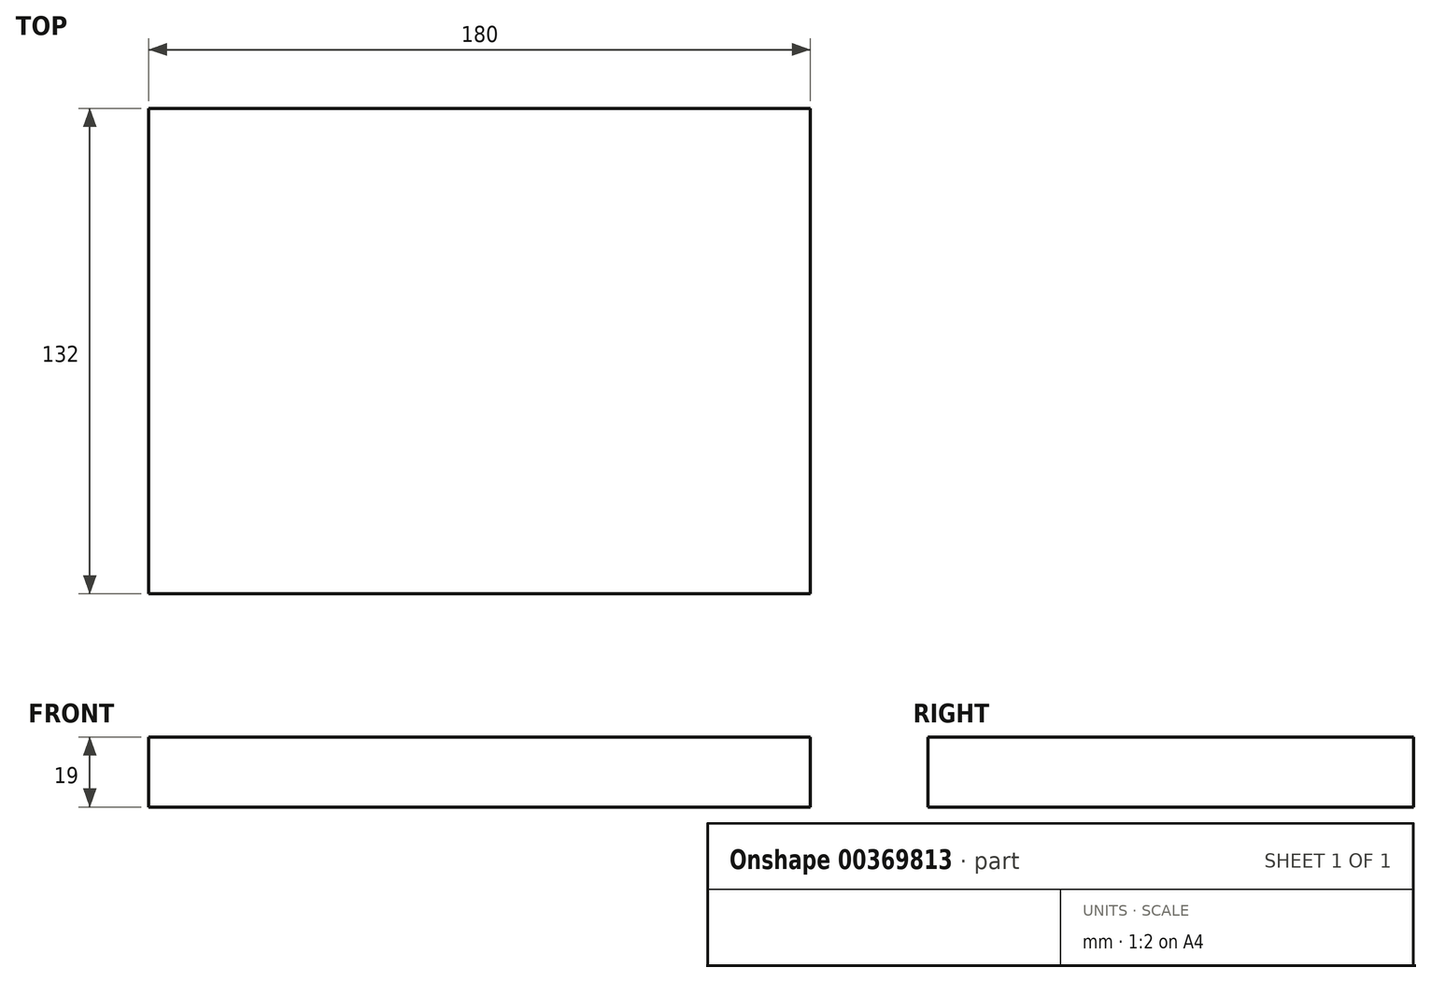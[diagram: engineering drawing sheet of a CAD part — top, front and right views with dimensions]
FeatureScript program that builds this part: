
annotation { "Feature Type Name" : "Feature", "Feature Type Description" : "" }
export const myFeature = defineFeature(function(context is Context, id is Id, definition is map)
    precondition{}
    {
        {
            var Q0;
            Q0=qCreatedBy(makeId("Top.planeOp"),FACE);
            var sketch = newSketch(context, id + "F0", { "sketchPlane" : qUnion([Q0])});
            skLineSegment(sketch, "E0.bottom", {"start": v(0, 0) * mm, "end": v(180, 0) * mm});
            skLineSegment(sketch, "E0.top", {"start": v(0, 132) * mm, "end": v(180, 132) * mm});
            skLineSegment(sketch, "E0.left", {"start": v(0, 0) * mm, "end": v(0, 132) * mm});
            skLineSegment(sketch, "E0.right", {"start": v(180, 0) * mm, "end": v(180, 132) * mm});
            skSolve(sketch);
        }
        {
            var Q0;
            Q0=makeQuery(id+"F0.imprint","IMPRINT",FACE,{"disambiguationData":[TD([[makeQuery(id+"F0.imprint","IMPRINT",EDGE,{"derivedFrom":sQuery(id+"F0.wireOp",EDGE,"E0.bottom")}),1.0]])]});
            extrude(context, id + "F1", {"entities" : qUnion([Q0]), "depth" : 19 * mm});
        }
    });
